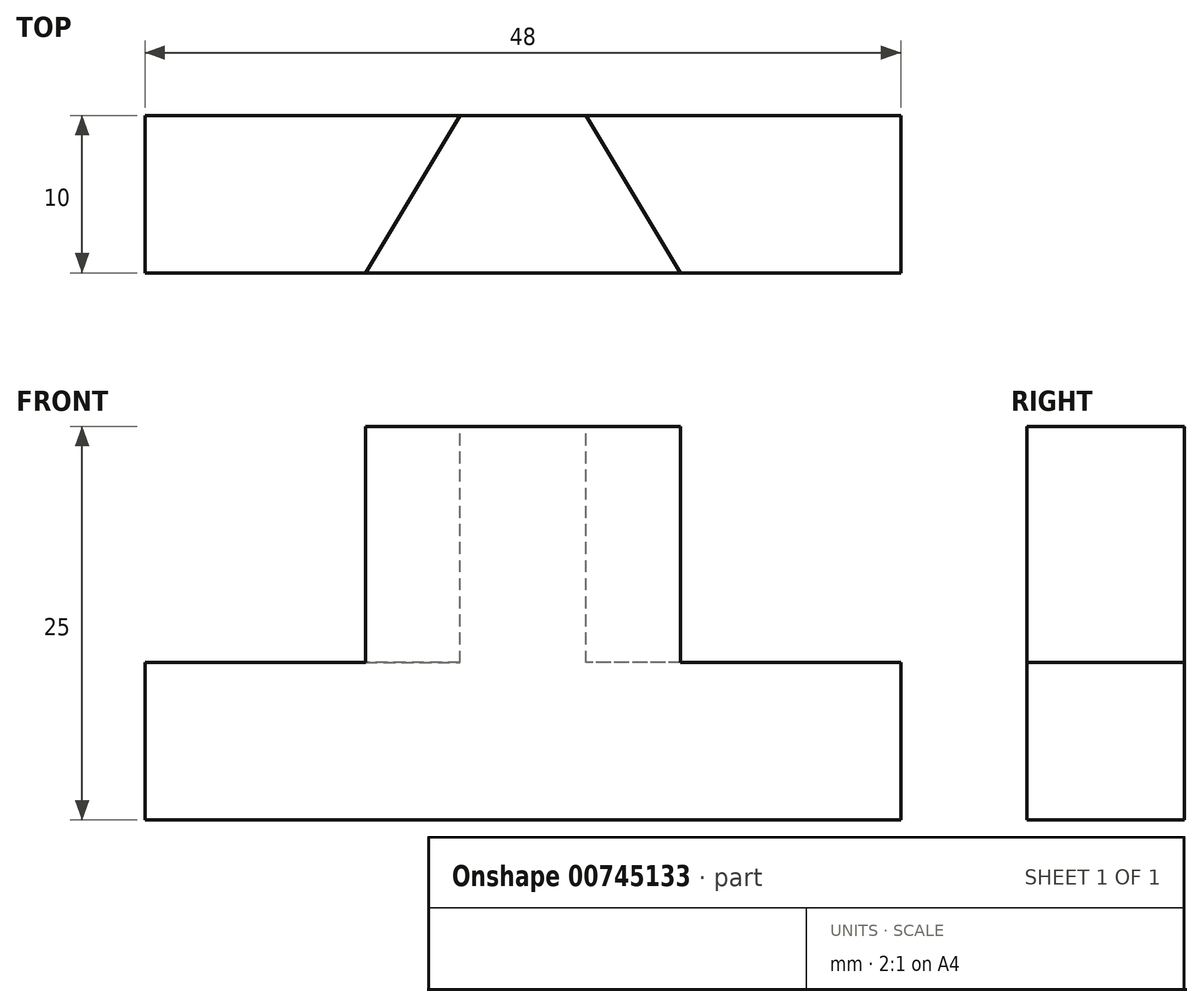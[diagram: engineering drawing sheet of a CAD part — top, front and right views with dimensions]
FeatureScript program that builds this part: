
annotation { "Feature Type Name" : "Feature", "Feature Type Description" : "" }
export const myFeature = defineFeature(function(context is Context, id is Id, definition is map)
    precondition{}
    {
        {
            var Q0;
            Q0=qCreatedBy(makeId("Front.planeOp"),FACE);
            var sketch = newSketch(context, id + "F0", { "sketchPlane" : qUnion([Q0])});
            skLineSegment(sketch, "E0.bottom", {"start": v(24, 12.5) * mm, "end": v(-24, 12.5) * mm});
            skLineSegment(sketch, "E0.top", {"start": v(24, -12.5) * mm, "end": v(-24, -12.5) * mm});
            skLineSegment(sketch, "E0.left", {"start": v(24, 12.5) * mm, "end": v(24, -12.5) * mm});
            skLineSegment(sketch, "E0.right", {"start": v(-24, 12.5) * mm, "end": v(-24, -12.5) * mm});
            skPoint(sketch, "E0.middle", {"position": v(0, 0) * mm});
            skSolve(sketch);
        }
        {
            var Q0;
            Q0 = qSketchRegion(id + "F0", true);
            extrude(context, id + "F1", {"entities" : qUnion([Q0]), "oppositeDirection" : true, "depth" : 10 * mm, "offsetDistance" : 25 * mm});
        }
        {
            var Q0;
            Q0=makeQuery(id+"F1.opExtrude","SWEPT_FACE",FACE,{"disambiguationData":[OSD([sQuery(id+"F0.wireOp",EDGE,"E0.bottom")])]});
            var sketch = newSketch(context, id + "F2", { "sketchPlane" : qUnion([Q0])});
            skLineSegment(sketch, "E1", {"start": v(0, 0) * mm, "end": v(10, 0) * mm});
            skLineSegment(sketch, "E2", {"start": v(10, 0) * mm, "end": v(4, 10) * mm});
            skLineSegment(sketch, "E3", {"start": v(4, 10) * mm, "end": v(0, 10) * mm});
            skLineSegment(sketch, "E4.MirrorCS", {"start": v(-4, 10) * mm, "end": v(0, 10) * mm});
            skLineSegment(sketch, "E5.MirrorCS", {"start": v(-10, 0) * mm, "end": v(-4, 10) * mm});
            skLineSegment(sketch, "E6.MirrorCS", {"start": v(0, 0) * mm, "end": v(-10, 0) * mm});
            skSolve(sketch);
        }
        {
            var Q0;
            {var subQ0=sQuery(id+"F2.wireOp",EDGE,"E5.MirrorCS");Q0=makeQuery(id+"F2.imprint","IMPRINT",FACE,{"disambiguationData":[TD([[makeQuery(id+"F2.imprint","IMPRINT",EDGE,{"derivedFrom":subQ0}),1.0]])]});}
            var Q1;
            {var subQ0=sQuery(id+"F2.wireOp",EDGE,"E2");Q1=makeQuery(id+"F2.imprint","IMPRINT",FACE,{"disambiguationData":[TD([[makeQuery(id+"F2.imprint","IMPRINT",EDGE,{"derivedFrom":subQ0}),-1.0]])]});}
            extrude(context, id + "F3", {"entities" : qUnion([Q0, Q1]), "operationType" : NewBodyOperationType.REMOVE, "oppositeDirection" : true, "depth" : 15 * mm, "offsetDistance" : 25 * mm});
        }
    });
